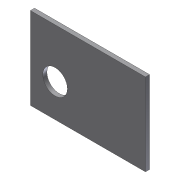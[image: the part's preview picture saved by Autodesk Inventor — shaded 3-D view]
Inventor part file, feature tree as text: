
AUTODESK INVENTOR PART (.ipt)
format: ipt  version: 2012 (Build 160160000, 160)  size: 81,408 bytes
history: native  units: in
note: dims shown in document units (in); Inventor stores cm internally (conversion verified against a paired STEP export)
features: extrude x2, sketch x2
ambient origin geometry x8: Origin, YZ Plane, XZ Plane, XY Plane, X Axis, Y Axis, Z Axis, Center Point
bodies: Solid1 (feature_tree)
feature tree (4):
  extrude  "Extrusion1"  Depth=2.5in
  extrude  "Extrusion2"  Depth=0.75in
  sketch  "Sketch1"  dims[d0=3.5in d1=2.5in]
  sketch  "Sketch2"  dims[d2=0.125in d3=0.0in d4=0.75in d5=0.75in d6=1.0in d7=0.125in d8=0.0in]
